FCSTD DOCUMENT  (FreeCAD 1.0R39319 (Git))
Label: clamp1
License: All rights reserved
LicenseURL: https://en.wikipedia.org/wiki/All_rights_reserved
objects: App::Link×7, App::FeaturePython×7, Assembly::JointGroup×1, Assembly::AssemblyObject×1
EXTERNAL_REF file=clamp.FCStd obj=Body
EXTERNAL_REF file=rec part.FCStd obj=Extrude001
EXTERNAL_REF file=screw.FCStd obj=Screw
EXTERNAL_REF file=nut.FCStd obj=Nut

FEATURE [App::Link] Body
  LinkedObject = -> <external clamp.FCStd>#Body
FEATURE [App::FeaturePython] GroundedJoint  # Assembly grounded joint (typed FeaturePython)
  ObjectToGround = -> Body
FEATURE [App::Link] Body001
  LinkPlacement = pos=(7e-16,-3,10) rot=(1,0,0;3.14159rad)
  LinkedObject = -> <external clamp.FCStd>#Body
  Placement = pos=(7e-16,-3,10) rot=(1,0,0;3.14159rad)
FEATURE [App::Link] Extrude001
  LinkPlacement = pos=(-25,-3,-30) rot=(0.57735,-0.57735,-0.57735;4.18879rad)
  LinkedObject = -> <external rec part.FCStd>#Extrude001
  Placement = pos=(-25,-3,-30) rot=(0.57735,-0.57735,-0.57735;4.18879rad)
FEATURE [App::Link] M5x12_Screw  label="M5x12-Screw"
  LinkPlacement = pos=(-25,3.35,5) rot=(-0.941969,-0.237376,-0.237376;1.63054rad)
  LinkedObject = -> <external screw.FCStd>#Screw
  Placement = pos=(-25,3.35,5) rot=(-0.941969,-0.237376,-0.237376;1.63054rad)
FEATURE [App::Link] M5x12_Screw001  label="M5x12-Screw001"
  LinkPlacement = pos=(25,2.35,5) rot=(0.510153,0.608171,0.608171;4.08507rad)
  LinkedObject = -> <external screw.FCStd>#Screw
  Placement = pos=(25,2.35,5) rot=(0.510153,0.608171,0.608171;4.08507rad)
FEATURE [App::Link] M5_Nut  label="M5-Nut"
  LinkPlacement = pos=(-25,-10.7,5) rot=(0.483548,0.618943,0.618943;4.04239rad)
  LinkedObject = -> <external nut.FCStd>#Nut
  Placement = pos=(-25,-10.7,5) rot=(0.483548,0.618943,0.618943;4.04239rad)
FEATURE [App::Link] M5_Nut001  label="M5-Nut001"
  LinkPlacement = pos=(25,-10.7,5) rot=(0.984948,0.122225,0.122225;4.69722rad)
  LinkedObject = -> <external nut.FCStd>#Nut
  Placement = pos=(25,-10.7,5) rot=(0.984948,0.122225,0.122225;4.69722rad)
FEATURE [App::FeaturePython] Joint  label="Fixed"  # Assembly joint (typed FeaturePython)
  Activated = true
  AngleMax = 0
  AngleMin = 0
  Detach1 = false
  Detach2 = false
  Distance = 0
  Distance2 = 0
  EnableAngleMax = false
  EnableAngleMin = false
  EnableLengthMax = false
  EnableLengthMin = false
  JointType = 0 (Fixed)
  LengthMax = 0
  LengthMin = 0
  Offset2 = pos=(0,0,0) rot=(0,0,1;1.5708rad)
  Placement1 = pos=(-25,0,5) rot=(0,0.707107,0.707107;3.14159rad)
  Placement2 = pos=(-35,-7.1e-15,3) rot=(0,0,-1;4.71239rad)
  Reference1 = -> Assembly [Body.Edge32,Body.Edge32]
  Reference2 = -> Assembly [Extrude001.Edge15,Extrude001.Edge15]
FEATURE [App::FeaturePython] Joint001  label="Fixed001"  # Assembly joint (typed FeaturePython)
  Activated = true
  AngleMax = 0
  AngleMin = 0
  Detach1 = false
  Detach2 = false
  Distance = 0
  Distance2 = 0
  EnableAngleMax = false
  EnableAngleMin = false
  EnableLengthMax = false
  EnableLengthMin = false
  JointType = 0 (Fixed)
  LengthMax = 0
  LengthMin = 0
  Offset2 = pos=(0,0,0) rot=(0,0,1;1.5708rad)
  Placement1 = pos=(-35,-7.1e-15,1.8e-15) rot=(0,0,1;0rad)
  Placement2 = pos=(-25,-4e-16,5) rot=(0.57735,0.57735,0.57735;4.18879rad)
  Reference1 = -> Assembly [Extrude001.Edge14,Extrude001.Edge14]
  Reference2 = -> Assembly [Body001.Edge32,Body001.Edge32]
FEATURE [App::FeaturePython] Joint002  label="Revolute"  # Assembly joint (typed FeaturePython)
  Activated = true
  AngleMax = 0
  AngleMin = 0
  Detach1 = false
  Detach2 = false
  Distance = 0
  Distance2 = 0
  EnableAngleMax = false
  EnableAngleMin = false
  EnableLengthMax = false
  EnableLengthMin = false
  JointType = 1 (Revolute)
  LengthMax = 0
  LengthMin = 0
  Offset2 = pos=(0,0,4) rot=(0,0,1;0rad)
  Placement1 = pos=(0,3.6e-15,3.65) rot=(0,0,1;0rad)
  Placement2 = pos=(-25,7,5) rot=(0,0.707107,0.707107;3.14159rad)
  Reference1 = -> Assembly [M5x12_Screw.Edge1,M5x12_Screw.Edge1]
  Reference2 = -> Assembly [Body.Edge12,Body.Edge12]
FEATURE [App::FeaturePython] Joint003  label="Revolute001"  # Assembly joint (typed FeaturePython)
  Activated = true
  AngleMax = 0
  AngleMin = 0
  Detach1 = false
  Detach2 = false
  Distance = 0
  Distance2 = 0
  EnableAngleMax = false
  EnableAngleMin = false
  EnableLengthMax = false
  EnableLengthMin = false
  JointType = 1 (Revolute)
  LengthMax = 0
  LengthMin = 0
  Placement1 = pos=(-1.8e-15,0,4.7) rot=(0,0,1;0rad)
  Placement2 = pos=(-25,3,5) rot=(0,0.707107,0.707107;3.14159rad)
  Reference1 = -> Assembly [M5_Nut.Edge7,M5_Nut.Edge7]
  Reference2 = -> Assembly [Body001.Edge12,Body001.Edge12]
FEATURE [App::FeaturePython] Joint004  label="Revolute002"  # Assembly joint (typed FeaturePython)
  Activated = true
  AngleMax = 0
  AngleMin = 0
  Detach1 = false
  Detach2 = false
  Distance = 0
  Distance2 = 0
  EnableAngleMax = false
  EnableAngleMin = false
  EnableLengthMax = false
  EnableLengthMin = false
  JointType = 1 (Revolute)
  LengthMax = 0
  LengthMin = 0
  Offset2 = pos=(0,0,6) rot=(0,0,1;0rad)
  Placement1 = pos=(0,0,3.65) rot=(0,-1,0;3.14159rad)
  Placement2 = pos=(25,6,5) rot=(0,0.707107,0.707107;3.14159rad)
  Reference1 = -> Assembly [M5x12_Screw001.Edge2,M5x12_Screw001.Edge2]
  Reference2 = -> Assembly [Body.Edge29,Body.Edge29]
FEATURE [App::FeaturePython] Joint005  label="Revolute003"  # Assembly joint (typed FeaturePython)
  Activated = true
  AngleMax = 0
  AngleMin = 0
  Detach1 = false
  Detach2 = false
  Distance = 0
  Distance2 = 0
  EnableAngleMax = false
  EnableAngleMin = false
  EnableLengthMax = false
  EnableLengthMin = false
  JointType = 1 (Revolute)
  LengthMax = 0
  LengthMin = 0
  Placement1 = pos=(0,0,4.7) rot=(0,0,1;0rad)
  Placement2 = pos=(25,3,5) rot=(0,0.707107,0.707107;3.14159rad)
  Reference1 = -> Assembly [M5_Nut001.Edge7,M5_Nut001.Edge7]
  Reference2 = -> Assembly [Body001.Edge8,Body001.Edge8]
FEATURE [Assembly::JointGroup] Joints
  Group = -> [GroundedJoint,Joint,Joint001,Joint002,Joint003,Joint004,Joint005]
FEATURE [Assembly::AssemblyObject] Assembly
  Group = -> [Joints,Body,GroundedJoint,Body001,Extrude001,M5x12_Screw,M5x12_Screw001,M5_Nut,M5_Nut001,Joint,Joint001,Joint002,Joint003,Joint004,Joint005]
  Origin = -> Origin
  Type = Assembly

RESOLVED EXTERNAL PARTS (link-assembly join: the EXTERNAL_REF files above that resolve inside this repo's crawl, each included once):
---- part clamp.FCStd = doc fcstd_c145d5d67536 ----
FCSTD DOCUMENT  (FreeCAD 1.0R39319 (Git))
Label: clamp
License: All rights reserved
LicenseURL: https://en.wikipedia.org/wiki/All_rights_reserved
objects: Sketcher::SketchObject×2, PartDesign::Pad×1, PartDesign::Pocket×1, PartDesign::Body×1
note: 11 computed .brp shape members not serialized (recipe doc carries the construction recipe); baked Part::Feature solids carry a one-line shape summary decoded from their .brp

FEATURE [Sketcher::SketchObject] Sketch
  ArcFitTolerance = 1e-06
  AttachmentSupport = -> [XY_Plane]
  FullyConstrained = true
  MakeInternals = false
  MapMode = 5
  sketch-geometry (10):
    g0: ArcOfCircle CenterX=0 CenterY=0 CenterZ=0 NormalX=0 NormalY=0 NormalZ=1 AngleXU=0 Radius=20.2237 StartAngle=0.14889 EndAngle=2.9927
    g1: ArcOfCircle CenterX=0 CenterY=0 CenterZ=0 NormalX=0 NormalY=0 NormalZ=1 AngleXU=0 Radius=17.2627 StartAngle=0.174672 EndAngle=2.96692
    g2: LineSegment StartX=-20 StartY=3 StartZ=0 EndX=-30 EndY=3 EndZ=0
    g3: LineSegment StartX=-30 StartY=3 StartZ=0 EndX=-30 EndY=0 EndZ=0
    g4: LineSegment StartX=-30 StartY=0 StartZ=0 EndX=-17 EndY=0 EndZ=0
    g5: LineSegment StartX=20 StartY=3 StartZ=0 EndX=30 EndY=3 EndZ=0
    g6: LineSegment StartX=30 StartY=3 StartZ=0 EndX=30 EndY=0 EndZ=0
    g7: LineSegment StartX=30 StartY=0 StartZ=0 EndX=17 EndY=0 EndZ=0
    g8: LineSegment StartX=-17 StartY=0 StartZ=0 EndX=-17 EndY=3 EndZ=0
    g9: LineSegment StartX=17 StartY=0 StartZ=0 EndX=17 EndY=3 EndZ=0
  constraints (30):
    c: Coincident(g0,g-1)
    c: Coincident(g1,g0)
    c: Horizontal(g2)
    c: Coincident(g3,g2)
    c: PointOnObject(g3,g-1)
    c: Vertical(g3)
    c: Coincident(g4,g3)
    c: Horizontal(g4)
    c: Horizontal(g5)
    c: Coincident(g6,g5)
    c: PointOnObject(g6,g-1)
    c: Vertical(g6)
    c: Coincident(g7,g6)
    c: Horizontal(g7)
    c: Equal(g2,g5)
    c: Equal(g3,g6)
    c: Coincident(g0,g2)
    c: Coincident(g0,g5)
    c: DistanceY(g3,g3) = 3
    c: DistanceX(g2,g2) = 10
    c: Distance(g6,g3) = 60
    c: DistanceX(g7,g0) = 3
    c: Coincident(g8,g4)
    c: Coincident(g8,g1)
    c: Coincident(g9,g7)
    c: Coincident(g9,g1)
    c: Vertical(g8)
    c: Vertical(g9)
    c: Horizontal(g0,g1)
    c: Horizontal(g0,g1)
FEATURE [PartDesign::Pad] Pad
  Direction = (0,0,1)
  Length = 10
  Length2 = 10
  Profile = -> Sketch
  ReferenceAxis = -> Sketch [N_Axis]
  Refine = true
  Suppressed = false
  Type = 0
FEATURE [Sketcher::SketchObject] Sketch001
  ArcFitTolerance = 1e-06
  AttachmentSupport = -> [Pad]
  ExternalGeometry = -> [Pad]
  FullyConstrained = true
  MakeInternals = false
  MapMode = 5
  Placement = pos=(0,3,0) rot=(0,0.707107,0.707107;3.14159rad)
  sketch-geometry (2):
    g0: Circle CenterX=-25 CenterY=5 CenterZ=0 NormalX=0 NormalY=0 NormalZ=1 AngleXU=0 Radius=2.5
    g1: Circle CenterX=25 CenterY=5 CenterZ=0 NormalX=0 NormalY=0 NormalZ=1 AngleXU=0 Radius=2.5
  constraints (4):
    c: Diameter(g0) = 5
    c: Symmetric(g-3,g-4,g0)
    c: Diameter(g1) = 5
    c: Symmetric(g-5,g-6,g1)
FEATURE [PartDesign::Pocket] Pocket
  BaseFeature = -> Pad
  Direction = (0,-1,2e-16)
  Length = 5
  Length2 = 5
  Profile = -> Sketch001
  ReferenceAxis = -> Sketch001 [N_Axis]
  Refine = true
  Suppressed = false
  Type = 1
FEATURE [PartDesign::Body] Body
  AllowCompound = false
  Group = -> [Sketch,Pad,Sketch001,Pocket]
  Origin = -> Origin
  Tip = -> Pocket
